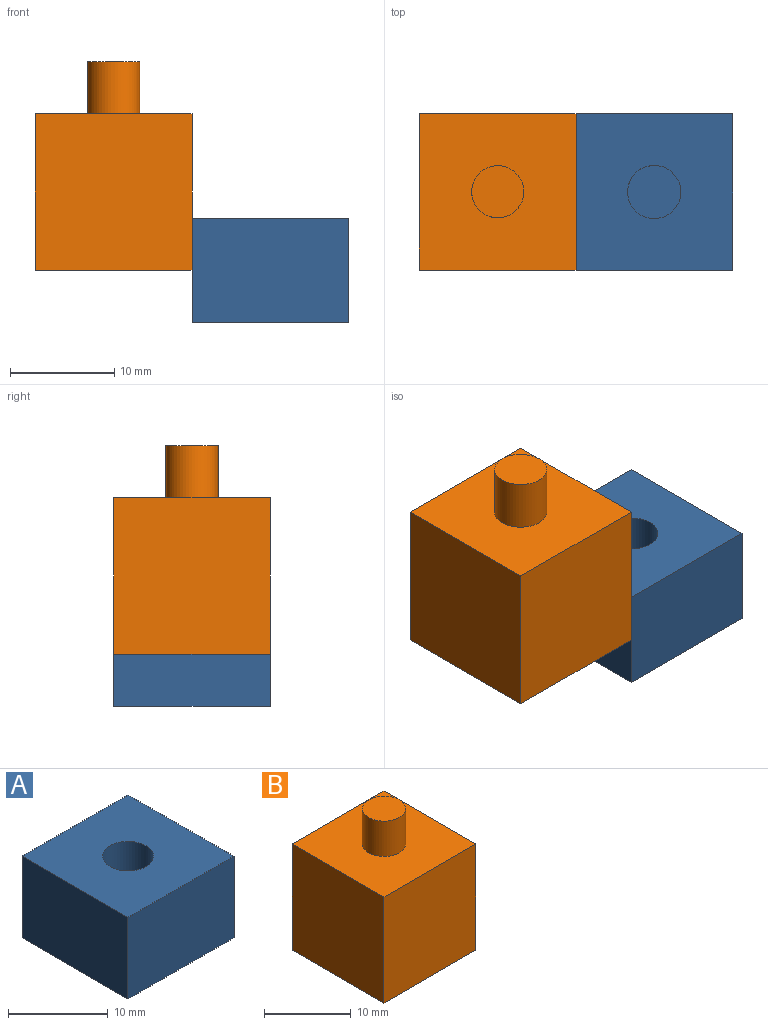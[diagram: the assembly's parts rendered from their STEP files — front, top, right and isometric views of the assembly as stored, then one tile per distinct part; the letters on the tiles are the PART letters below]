
ASSEMBLY  parts=2 mates=1
PART A: 8 faces, bbox 15x15x10 mm
  f0: plane 15x10mm, normal (1,0,0), area 150mm2, adj f1,f3,f4,f5
  f1: plane 15x10mm, normal (0,1,0), area 150mm2, adj f0,f2,f4,f5
  f2: plane 15x10mm, normal (-1,0,0), area 150mm2, adj f1,f3,f4,f5
  f3: plane 15x10mm, normal (0,-1,0), area 150mm2, adj f0,f2,f4,f5
  f4: plane 15x15mm, normal (0,0,1), area 204.6mm2, adj f0,f1,f2,f3,f6
  f5: plane 15x15mm, normal (0,0,-1), area 225mm2, adj f0,f1,f2,f3
  f6: cylinder r=2.55mm len=5.1mm, axis (0,0,1), area 80.1mm2, adj f4,f7
  f7: plane 5.1x5.1mm, normal (0,0,1), area 20.4mm2, adj f6
PART B: 8 faces, bbox 15x15x20 mm
  f0: plane 15x15mm, normal (1,0,0), area 225mm2, adj f1,f3,f4,f5
  f1: plane 15x15mm, normal (0,1,0), area 225mm2, adj f0,f2,f4,f5
  f2: plane 15x15mm, normal (-1,0,0), area 225mm2, adj f1,f3,f4,f5
  f3: plane 15x15mm, normal (0,-1,0), area 225mm2, adj f0,f2,f4,f5
  f4: plane 15x15mm, normal (0,0,1), area 205.4mm2, adj f0,f1,f2,f3,f6
  f5: plane 15x15mm, normal (0,0,-1), area 225mm2, adj f0,f1,f2,f3
  f6: cylinder r=2.5mm len=5mm, axis (0,0,-1), area 78.5mm2, adj f4,f7
  f7: plane 5x5mm, normal (0,0,1), area 19.6mm2, adj f6
PLACE A t=(1.31,-9.47,11.87)mm
PLACE B rot(axis=(0,0,1),180deg) t=(-13.69,-9.47,16.87)mm
MATE planar B.f2 <-> A.f2  axis (1,0,0) through (-6.19,-9.47,16.87)mm
